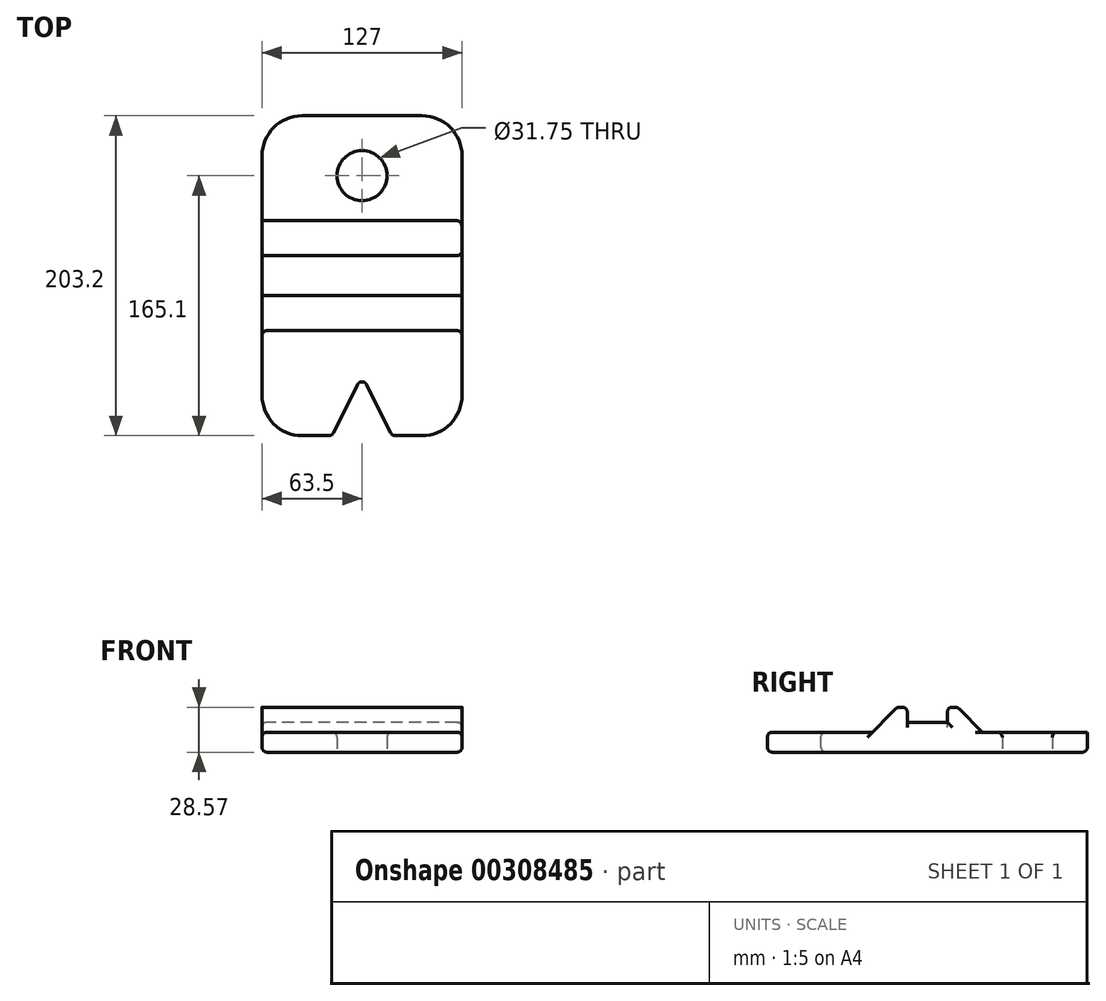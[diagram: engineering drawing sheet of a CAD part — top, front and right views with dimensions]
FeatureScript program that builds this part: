
annotation { "Feature Type Name" : "Feature", "Feature Type Description" : "" }
export const myFeature = defineFeature(function(context is Context, id is Id, definition is map)
    precondition{}
    {
        {
            var Q0;
            Q0=qCreatedBy(makeId("Top.planeOp"),FACE);
            var sketch = newSketch(context, id + "F0", { "sketchPlane" : qUnion([Q0])});
            skLineSegment(sketch, "E0.bottom", {"start": v(-63.5, 63.5) * mm, "end": v(63.5, 63.5) * mm});
            skLineSegment(sketch, "E0.top", {"start": v(-63.5, -139.7) * mm, "end": v(63.5, -139.7) * mm});
            skLineSegment(sketch, "E0.left", {"start": v(-63.5, 63.5) * mm, "end": v(-63.5, -139.7) * mm});
            skLineSegment(sketch, "E0.right", {"start": v(63.5, 63.5) * mm, "end": v(63.5, -139.7) * mm});
            skSolve(sketch);
        }
        {
            var Q0;
            Q0=qSketchRegion(id+"F0",true);
            extrude(context, id + "F1", {"entities" : qUnion([Q0]), "depth" : 12.7 * mm});
        }
        {
            var Q0;
            Q0=qCreatedBy(makeId("Top.planeOp"),FACE);
            var sketch = newSketch(context, id + "F2", { "sketchPlane" : qUnion([Q0])});
            skCircle(sketch, "E1", {"center": v(0, 25.4) * mm, "radius": 15.88 * mm});
            skSolve(sketch);
        }
        {
            var Q0;
            Q0=qSketchRegion(id+"F2",true);
            extrude(context, id + "F3", {"entities" : qUnion([Q0]), "operationType" : NewBodyOperationType.REMOVE, "depth" : 25.4 * mm});
        }
        {
            var Q0;
            Q0=qCreatedBy(makeId("Top.planeOp"),FACE);
            var sketch = newSketch(context, id + "F4", { "sketchPlane" : qUnion([Q0])});
            skLineSegment(sketch, "E2", {"start": v(0, -101.6) * mm, "end": v(-38.1, -177.8) * mm});
            skLineSegment(sketch, "E3", {"start": v(-38.1, -177.8) * mm, "end": v(38.1, -177.8) * mm});
            skLineSegment(sketch, "E4", {"start": v(38.1, -177.8) * mm, "end": v(0, -101.6) * mm});
            skSolve(sketch);
        }
        {
            var Q0;
            Q0=qSketchRegion(id+"F4",true);
            extrude(context, id + "F5", {"entities" : qUnion([Q0]), "operationType" : NewBodyOperationType.REMOVE, "depth" : 25.4 * mm});
        }
        {
            var Q0;
            Q0=qCreatedBy(makeId("Right.planeOp"),FACE);
            var sketch = newSketch(context, id + "F6", { "sketchPlane" : qUnion([Q0])});
            skLineSegment(sketch, "E5", {"start": v(-19.05, 28.57) * mm, "end": v(-25.4, 28.57) * mm});
            skLineSegment(sketch, "E6", {"start": v(-25.4, 28.57) * mm, "end": v(-25.4, 19.05) * mm});
            skLineSegment(sketch, "E7", {"start": v(-25.4, 19.05) * mm, "end": v(-50.8, 19.05) * mm});
            skLineSegment(sketch, "E8", {"start": v(-50.8, 19.05) * mm, "end": v(-50.8, 28.57) * mm});
            skLineSegment(sketch, "E9", {"start": v(-50.8, 28.57) * mm, "end": v(-57.15, 28.57) * mm});
            skLineSegment(sketch, "E10", {"start": v(-85.72, 0) * mm, "end": v(9.52, 0) * mm});
            skLineSegment(sketch, "E11", {"start": v(-19.05, 28.58) * mm, "end": v(9.53, 0) * mm});
            skLineSegment(sketch, "E12", {"start": v(-57.15, 28.58) * mm, "end": v(-85.72, 0) * mm});
            skSolve(sketch);
        }
        {
            var Q0;
            Q0=qSketchRegion(id+"F6",true);
            extrude(context, id + "F7", {"entities" : qUnion([Q0]), "operationType" : NewBodyOperationType.ADD, "depth" : 63.5 * mm, "hasSecondDirection" : true, "secondDirectionOppositeDirection" : true, "secondDirectionDepth" : 63.5 * mm});
        }
        {
            var Q0;
            Q0=makeQuery(id+"F1.opExtrude","SWEPT_EDGE",EDGE,{"disambiguationData":[OSD([sQuery(id+"F0.wireOp",EDGE,"E0.top"),sQuery(id+"F0.wireOp",EDGE,"E0.right")])]});
            var Q1;
            Q1=makeQuery(id+"F1.opExtrude","SWEPT_EDGE",EDGE,{"disambiguationData":[OSD([sQuery(id+"F0.wireOp",EDGE,"E0.top"),sQuery(id+"F0.wireOp",EDGE,"E0.left")])]});
            var Q2;
            Q2=makeQuery(id+"F1.opExtrude","SWEPT_EDGE",EDGE,{"disambiguationData":[OSD([sQuery(id+"F0.wireOp",EDGE,"E0.bottom"),sQuery(id+"F0.wireOp",EDGE,"E0.left")])]});
            var Q3;
            Q3=makeQuery(id+"F1.opExtrude","SWEPT_EDGE",EDGE,{"disambiguationData":[OSD([sQuery(id+"F0.wireOp",EDGE,"E0.bottom"),sQuery(id+"F0.wireOp",EDGE,"E0.right")])]});
            fillet(context, id + "F8", {"entities" : qUnion([Q0, Q1, Q2, Q3]), "radius" : 25.4 * mm, "tangentPropagation" : true, "allowEdgeOverflow" : false});
        }
        {
            var Q0;
            Q0=makeQuery(id+"F5.boolean.opBoolean","INTERSECT",EDGE,{"derivedFrom":[makeQuery(id+"F1.opExtrude","SWEPT_FACE",FACE,{"disambiguationData":[OSD([sQuery(id+"F0.wireOp",EDGE,"E0.top")])]}),makeQuery(id+"F5.opExtrude","SWEPT_FACE",FACE,{"disambiguationData":[OSD([sQuery(id+"F4.wireOp",EDGE,"E2")])]})]});
            var Q1;
            Q1=makeQuery(id+"F5.boolean.opBoolean","INTERSECT",EDGE,{"derivedFrom":[makeQuery(id+"F1.opExtrude","SWEPT_FACE",FACE,{"disambiguationData":[OSD([sQuery(id+"F0.wireOp",EDGE,"E0.top")])]}),makeQuery(id+"F5.opExtrude","SWEPT_FACE",FACE,{"disambiguationData":[OSD([sQuery(id+"F4.wireOp",EDGE,"E4")])]})]});
            var Q2;
            Q2=makeQuery(id+"F5.boolean.opBoolean","COPY",EDGE,{"derivedFrom":makeQuery(id+"F5.opExtrude","SWEPT_EDGE",EDGE,{"disambiguationData":[OSD([sQuery(id+"F4.wireOp",EDGE,"E2"),sQuery(id+"F4.wireOp",EDGE,"E4")])]})});
            var Q3;
            Q3=makeQuery(id+"F7.boolean.opBoolean","INTERSECT",EDGE,{"derivedFrom":[makeQuery(id+"F1.opExtrude","CAP_FACE",FACE,{"disambiguationData":[OSD([sQuery(id+"F0.wireOp",EDGE,"E0.bottom"),sQuery(id+"F0.wireOp",EDGE,"E0.top"),sQuery(id+"F0.wireOp",EDGE,"E0.left"),sQuery(id+"F0.wireOp",EDGE,"E0.right")])],"isStart":false}),makeQuery(id+"F7.opExtrude","SWEPT_FACE",FACE,{"disambiguationData":[OSD([sQuery(id+"F6.wireOp",EDGE,"knqkPp9u-nINb-6zL6-6JZt-FZVEQR52XJbq")])]})]});
            var Q4;
            Q4=makeQuery(id+"F7.opExtrude","SWEPT_EDGE",EDGE,{"disambiguationData":[OSD([sQuery(id+"F6.wireOp",EDGE,"E9"),sQuery(id+"F6.wireOp",EDGE,"knqkPp9u-nINb-6zL6-6JZt-FZVEQR52XJbq")])]});
            var Q5;
            Q5=makeQuery(id+"F7.opExtrude","SWEPT_EDGE",EDGE,{"disambiguationData":[OSD([sQuery(id+"F6.wireOp",EDGE,"E8"),sQuery(id+"F6.wireOp",EDGE,"E9")])]});
            var Q6;
            Q6=makeQuery(id+"F7.boolean.opBoolean","INTERSECT",EDGE,{"derivedFrom":[makeQuery(id+"F1.opExtrude","CAP_FACE",FACE,{"disambiguationData":[OSD([sQuery(id+"F0.wireOp",EDGE,"E0.bottom"),sQuery(id+"F0.wireOp",EDGE,"E0.top"),sQuery(id+"F0.wireOp",EDGE,"E0.left"),sQuery(id+"F0.wireOp",EDGE,"E0.right")])],"isStart":false}),makeQuery(id+"F7.opExtrude","SWEPT_FACE",FACE,{"disambiguationData":[OSD([sQuery(id+"F6.wireOp",EDGE,"E6")])]})]});
            var Q7;
            Q7=makeQuery(id+"F7.opExtrude","SWEPT_EDGE",EDGE,{"disambiguationData":[OSD([sQuery(id+"F6.wireOp",EDGE,"E5"),sQuery(id+"F6.wireOp",EDGE,"E6")])]});
            var Q8;
            Q8=makeQuery(id+"F7.opExtrude","SWEPT_EDGE",EDGE,{"disambiguationData":[OSD([sQuery(id+"F6.wireOp",EDGE,"YxGyQr56-0Cs3-wmJc-XaXd-A3KuC3WRsn8x"),sQuery(id+"F6.wireOp",EDGE,"E5")])]});
            var Q9;
            Q9=makeQuery(id+"F7.boolean.opBoolean","INTERSECT",EDGE,{"derivedFrom":[makeQuery(id+"F1.opExtrude","CAP_FACE",FACE,{"disambiguationData":[OSD([sQuery(id+"F0.wireOp",EDGE,"E0.bottom"),sQuery(id+"F0.wireOp",EDGE,"E0.top"),sQuery(id+"F0.wireOp",EDGE,"E0.left"),sQuery(id+"F0.wireOp",EDGE,"E0.right")])],"isStart":false}),makeQuery(id+"F7.opExtrude","SWEPT_FACE",FACE,{"disambiguationData":[OSD([sQuery(id+"F6.wireOp",EDGE,"E8")])]})]});
            var Q10;
            Q10=makeQuery(id+"F7.boolean.opBoolean","INTERSECT",EDGE,{"derivedFrom":[makeQuery(id+"F1.opExtrude","CAP_FACE",FACE,{"disambiguationData":[OSD([sQuery(id+"F0.wireOp",EDGE,"E0.bottom"),sQuery(id+"F0.wireOp",EDGE,"E0.top"),sQuery(id+"F0.wireOp",EDGE,"E0.left"),sQuery(id+"F0.wireOp",EDGE,"E0.right")])],"isStart":false}),makeQuery(id+"F7.opExtrude","SWEPT_FACE",FACE,{"disambiguationData":[OSD([sQuery(id+"F6.wireOp",EDGE,"YxGyQr56-0Cs3-wmJc-XaXd-A3KuC3WRsn8x")])]})]});
            fillet(context, id + "F9", {"entities" : qUnion([Q0, Q1, Q2, Q3, Q4, Q5, Q6, Q7, Q8, Q9, Q10]), "radius" : 3.17 * mm, "tangentPropagation" : true, "allowEdgeOverflow" : false});
        }
        {
            var Q0;
            {var subQ0=sQuery(id+"F0.wireOp",EDGE,"E0.right");var subQ1=sQuery(id+"F0.wireOp",EDGE,"E0.left");var subQ2=sQuery(id+"F0.wireOp",EDGE,"E0.top");Q0=makeQuery(id+"F8.opFillet","BLEND_EDGE",EDGE,{"blendedFrom":[makeQuery(id+"F1.opExtrude","SWEPT_EDGE",EDGE,{"disambiguationData":[OSD([subQ2,subQ0])]}),makeQuery(id+"F7.boolean.opBoolean","SPLIT",FACE,{"disambiguationData":[TD([makeQuery(id+"F1.opExtrude","SWEPT_FACE",FACE,{"disambiguationData":[OSD([subQ2])]})])],"derivedFrom":makeQuery(id+"F1.opExtrude","CAP_FACE",FACE,{"disambiguationData":[OSD([sQuery(id+"F0.wireOp",EDGE,"E0.bottom"),subQ2,subQ1,subQ0])],"isStart":false})})],"blendedInto":[makeQuery(id+"F7.boolean.opBoolean","SPLIT",FACE,{"disambiguationData":[TD([makeQuery(id+"F1.opExtrude","SWEPT_FACE",FACE,{"disambiguationData":[OSD([subQ2])]})])],"derivedFrom":makeQuery(id+"F1.opExtrude","CAP_FACE",FACE,{"disambiguationData":[OSD([sQuery(id+"F0.wireOp",EDGE,"E0.bottom"),subQ2,subQ1,subQ0])],"isStart":false})})]});}
            var Q1;
            Q1=makeQuery(id+"F3.boolean.opBoolean","INTERSECT",EDGE,{"derivedFrom":[makeQuery(id+"F1.opExtrude","CAP_FACE",FACE,{"disambiguationData":[OSD([sQuery(id+"F0.wireOp",EDGE,"E0.bottom"),sQuery(id+"F0.wireOp",EDGE,"E0.top"),sQuery(id+"F0.wireOp",EDGE,"E0.left"),sQuery(id+"F0.wireOp",EDGE,"E0.right")])],"isStart":false}),makeQuery(id+"F3.opExtrude","SWEPT_FACE",FACE,{"disambiguationData":[OSD([sQuery(id+"F2.wireOp",EDGE,"E1")])]})]});
            var Q2;
            Q2=makeQuery(id+"F1.opExtrude","CAP_EDGE",EDGE,{"disambiguationData":[OSD([sQuery(id+"F0.wireOp",EDGE,"E0.right")])],"isStart":true});
            var Q3;
            Q3=makeQuery(id+"F3.boolean.opBoolean","COPY",EDGE,{"derivedFrom":makeQuery(id+"F3.opExtrude","CAP_EDGE",EDGE,{"disambiguationData":[OSD([sQuery(id+"F2.wireOp",EDGE,"E1")])],"isStart":true})});
            var Q4;
            Q4=makeQuery(id+"F7.opExtrude","CAP_EDGE",EDGE,{"disambiguationData":[OSD([sQuery(id+"F6.wireOp",EDGE,"E7")])],"isStart":false});
            var Q5;
            Q5=makeQuery(id+"F7.opExtrude","CAP_EDGE",EDGE,{"disambiguationData":[OSD([sQuery(id+"F6.wireOp",EDGE,"E6")])],"isStart":false});
            var Q6;
            Q6=makeQuery(id+"F7.opExtrude","CAP_EDGE",EDGE,{"disambiguationData":[OSD([sQuery(id+"F6.wireOp",EDGE,"E7")])],"isStart":true});
            fillet(context, id + "F10", {"entities" : qUnion([Q0, Q1, Q2, Q3, Q4, Q5, Q6]), "radius" : 3.17 * mm, "tangentPropagation" : true, "allowEdgeOverflow" : false});
        }
    });
